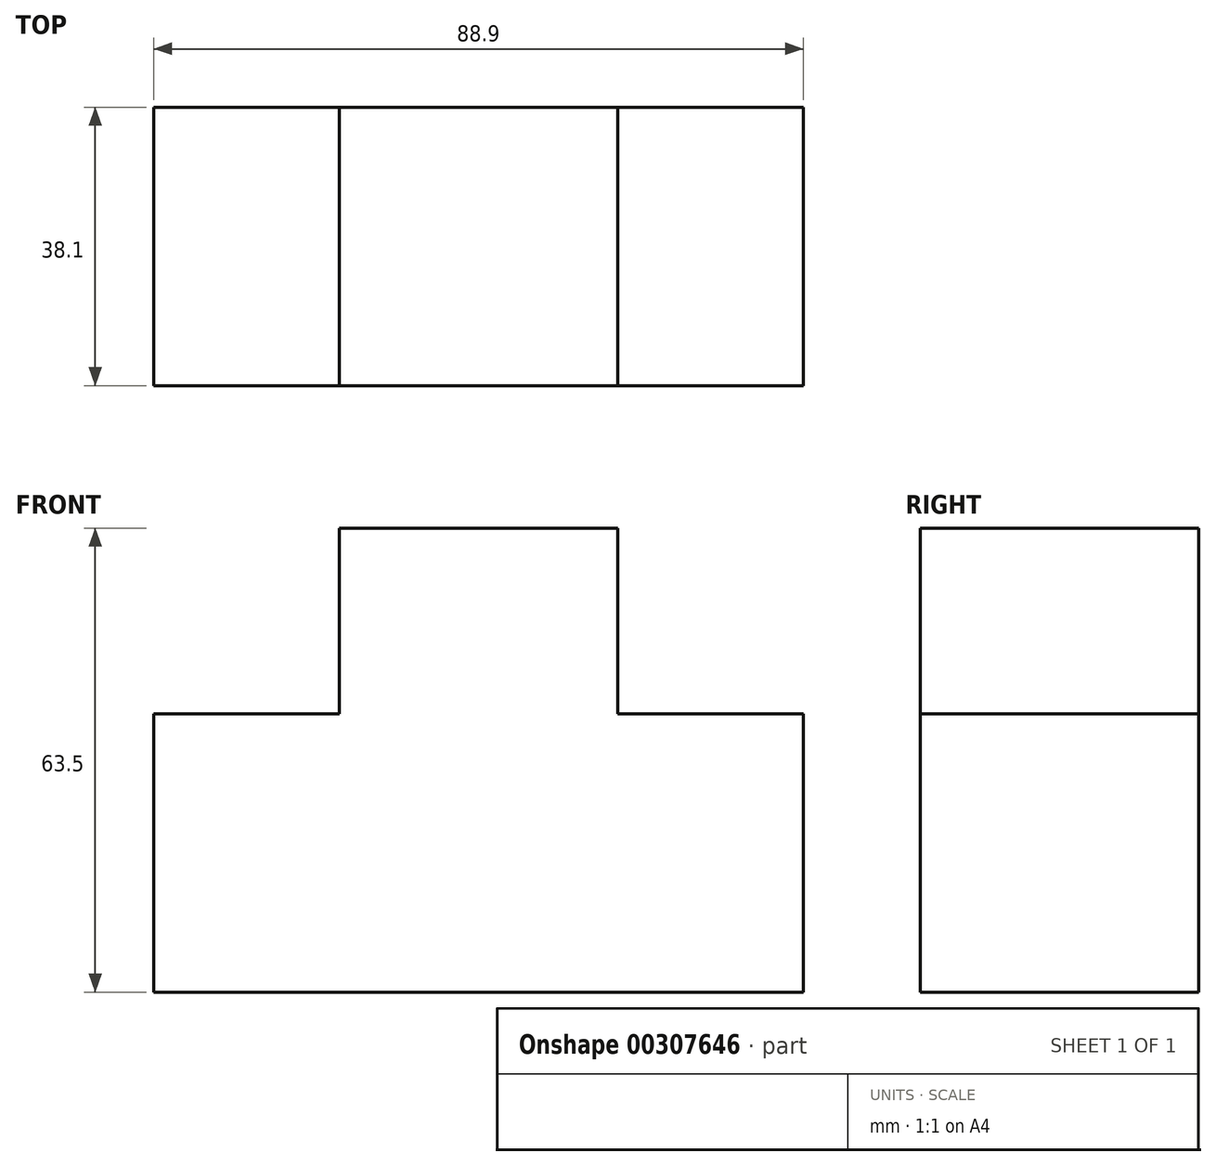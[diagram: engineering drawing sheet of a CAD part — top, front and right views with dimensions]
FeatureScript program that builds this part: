
annotation { "Feature Type Name" : "Feature", "Feature Type Description" : "" }
export const myFeature = defineFeature(function(context is Context, id is Id, definition is map)
    precondition{}
    {
        {
            var Q0;
            Q0=qCreatedBy(makeId("Front.planeOp"),FACE);
            var sketch = newSketch(context, id + "F0", { "sketchPlane" : qUnion([Q0])});
            skLineSegment(sketch, "E0", {"start": v(-53.02, -41.24) * mm, "end": v(35.88, -41.24) * mm});
            skLineSegment(sketch, "E1", {"start": v(35.88, -41.24) * mm, "end": v(35.88, -3.14) * mm});
            skLineSegment(sketch, "E2", {"start": v(35.88, -3.14) * mm, "end": v(10.48, -3.14) * mm});
            skLineSegment(sketch, "E3", {"start": v(10.48, -3.14) * mm, "end": v(10.48, 22.26) * mm});
            skLineSegment(sketch, "E4", {"start": v(10.48, 22.26) * mm, "end": v(-27.62, 22.26) * mm});
            skLineSegment(sketch, "E5", {"start": v(-27.62, 22.26) * mm, "end": v(-27.62, -3.14) * mm});
            skLineSegment(sketch, "E6", {"start": v(-27.62, -3.14) * mm, "end": v(-53.02, -3.14) * mm});
            skLineSegment(sketch, "E7", {"start": v(-53.02, -3.14) * mm, "end": v(-53.02, -41.24) * mm});
            skSolve(sketch);
        }
        {
            var Q0;
            Q0=makeQuery(id+"F0.imprint","IMPRINT",FACE,{"disambiguationData":[TD([[makeQuery(id+"F0.imprint","IMPRINT",EDGE,{"derivedFrom":sQuery(id+"F0.wireOp",EDGE,"E0")}),1.0]])]});
            extrude(context, id + "F1", {"entities" : qUnion([Q0]), "depth" : 38.1 * mm});
        }
    });
